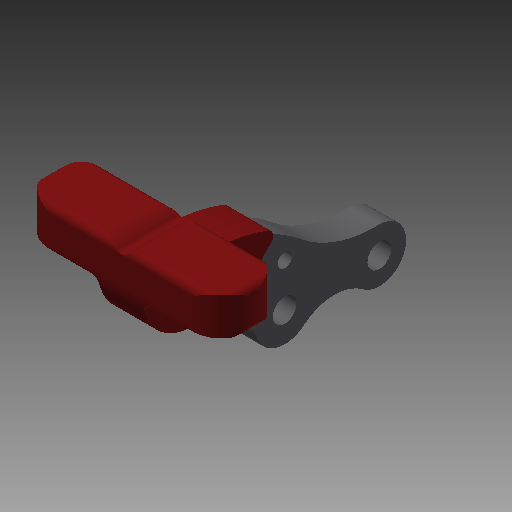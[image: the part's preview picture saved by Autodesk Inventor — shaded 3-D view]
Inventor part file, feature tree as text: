
AUTODESK INVENTOR PART (.ipt)
format: ipt  version: 2018 (Build 220112000, 112)  size: 234,496 bytes
history: native  units: mm
features: other x21, sketch x7, extrude x5, revolve x2
ambient origin geometry x8: Origin, YZ Plane, XZ Plane, XY Plane, X Axis, Y Axis, Z Axis, Center Point
bodies: Solid1 (feature_tree)
feature tree (35):
  extrude  "Extrusion1"  Depth=6.0mm TaperAngle=0.0deg
  extrude  "Extrusion2"  TaperAngle=360.0deg  [1 undecoded]
  revolve  "Revolution1"  [1 undecoded]
  revolve  "Revolution2"  [1 undecoded]
  extrude  "Extrusion3"  [1 undecoded]
  extrude  "Extrusion4"  [1 undecoded]
  extrude  "Extrusion5"  [1 undecoded]
  other  "HG1_XY"
  other  "HG1_YZ"
  other  "HG1_ZX"
  other  "HG1_X"
  other  "HG1_Y"
  other  "HG1_Z"
  other  "HG1_Center"
  other  "HG2_XY"
  other  "HG2_YZ"
  other  "HG2_ZX"
  other  "HG2_X"
  other  "HG2_Y"
  other  "HG2_Z"
  other  "HG2_Center"
  other  "HG3_XY"
  other  "HG3_YZ"
  other  "HG3_ZX"
  other  "HG3_X"
  other  "HG3_Y"
  other  "HG3_Z"
  other  "HG3_Center"
  sketch  "Skizze_4"
  sketch  "Sketch_1"  dims[d0=4.0mm d1=0.0mm d2=6.0mm d3=0.0mm]
  sketch  "Skizze_5_ALT_Drilling_1"  dims[d4=360.0deg d5=360.0deg]
  sketch  "Skizze_6_ALT_Drilling_2"  dims[d6=6.1mm d7=0.0mm d8=40.0mm d9=0.0mm]
  sketch  "Sketch_2"  dims[d10=10.0mm d11=0.0mm]
  sketch  "Sketch_3"
  sketch  "Sketch_4"
note: 6 required parameter values undecoded (feature->parameter linkage not recoverable at this tier; creation-order binding heuristic only, values carry confidence <= 0.55)